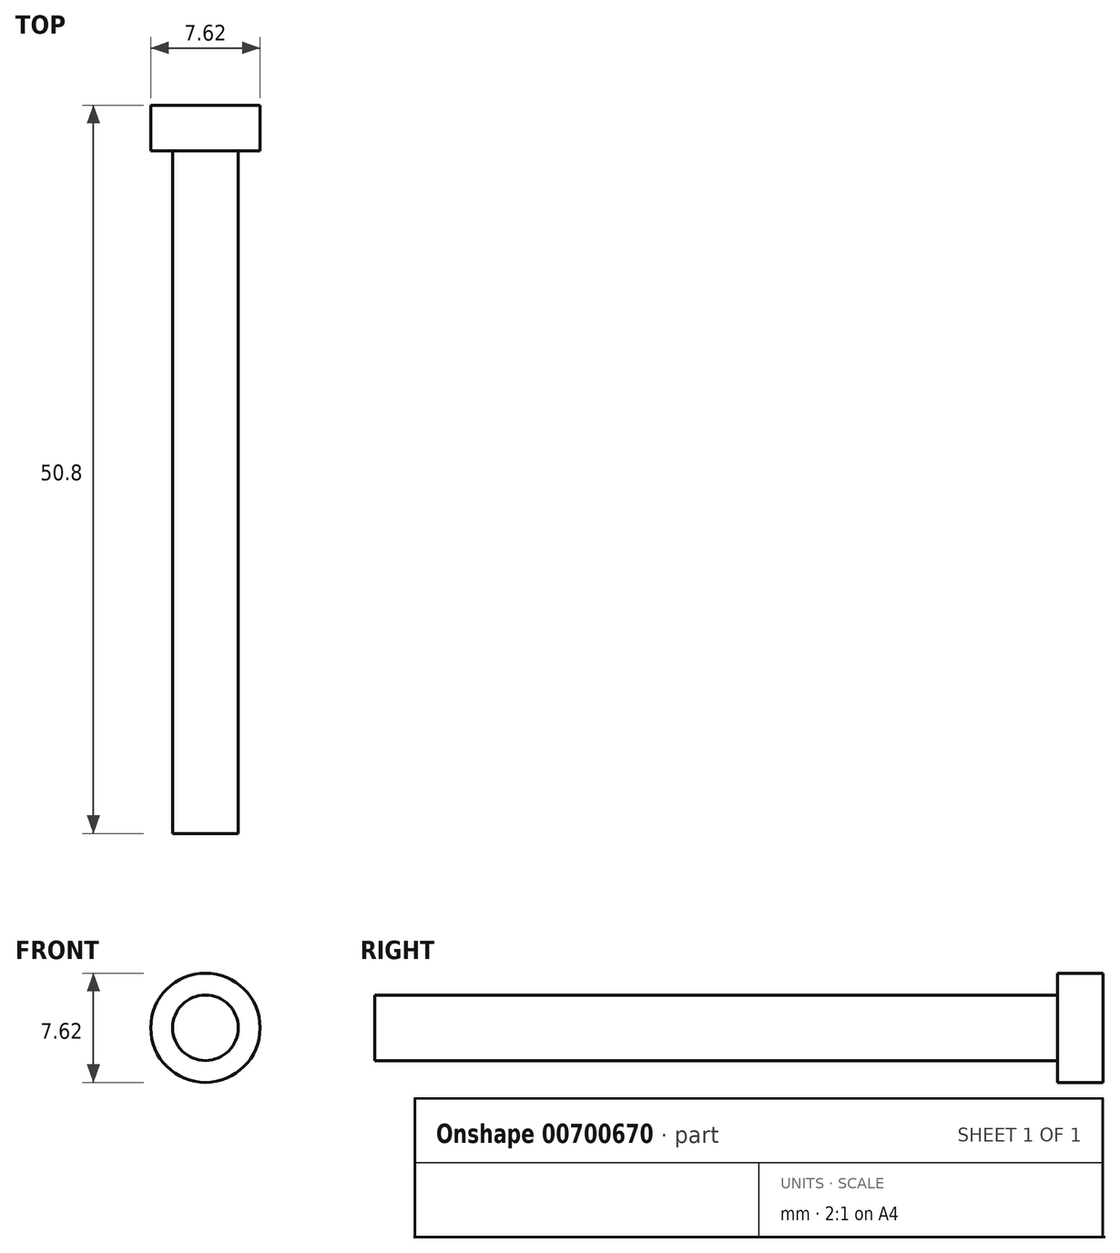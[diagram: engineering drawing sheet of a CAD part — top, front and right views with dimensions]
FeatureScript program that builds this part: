
annotation { "Feature Type Name" : "Feature", "Feature Type Description" : "" }
export const myFeature = defineFeature(function(context is Context, id is Id, definition is map)
    precondition{}
    {
        {
            var Q0;
            Q0=qCreatedBy(makeId("Front.planeOp"),FACE);
            var sketch = newSketch(context, id + "F0", { "sketchPlane" : qUnion([Q0])});
            skCircle(sketch, "E0", {"center": v(0, 0) * mm, "radius": 3.81 * mm});
            skSolve(sketch);
        }
        {
            var Q0;
            Q0 = qSketchRegion(id + "F0", true);
            extrude(context, id + "F1", {"entities" : qUnion([Q0]), "depth" : 50.8 * mm, "offsetDistance" : 25.4 * mm});
        }
        {
            var Q0;
            Q0=makeQuery(id+"F1.opExtrude","CAP_FACE",FACE,{"disambiguationData":[OSD([sQuery(id+"F0.wireOp",EDGE,"E0")])],"isStart":false});
            var sketch = newSketch(context, id + "F2", { "sketchPlane" : qUnion([Q0])});
            skCircle(sketch, "E1", {"center": v(0, 0) * mm, "radius": 2.29 * mm});
            skCircle(sketch, "E2", {"center": v(0, 0) * mm, "radius": 5.08 * mm});
            skSolve(sketch);
        }
        {
            var Q0;
            Q0 = qSketchRegion(id + "F2", true);
            extrude(context, id + "F3", {"entities" : qUnion([Q0]), "operationType" : NewBodyOperationType.REMOVE, "oppositeDirection" : true, "depth" : 47.62 * mm, "offsetDistance" : 25.4 * mm});
        }
    });
